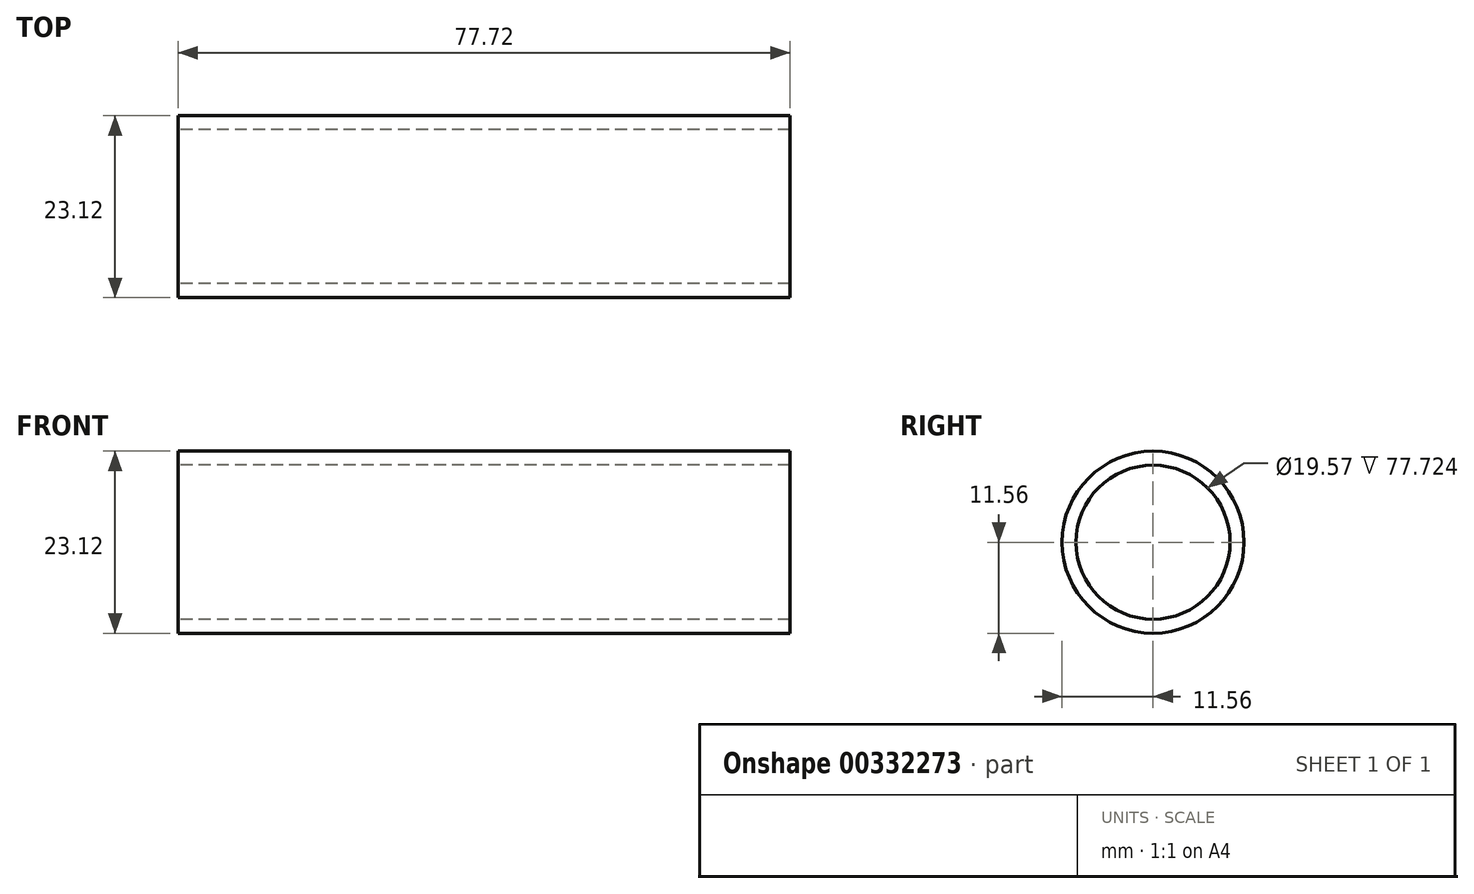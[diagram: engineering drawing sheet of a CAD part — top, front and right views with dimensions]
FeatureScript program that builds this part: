
annotation { "Feature Type Name" : "Feature", "Feature Type Description" : "" }
export const myFeature = defineFeature(function(context is Context, id is Id, definition is map)
    precondition{}
    {
        {
            var Q0;
            Q0=qCreatedBy(makeId("Right.planeOp"),FACE);
            var sketch = newSketch(context, id + "F0", { "sketchPlane" : qUnion([Q0])});
            skCircle(sketch, "E0", {"center": v(0, 0) * mm, "radius": 11.56 * mm});
            skCircle(sketch, "E1", {"center": v(0, 0) * mm, "radius": 9.78 * mm});
            skSolve(sketch);
        }
        {
            var Q0;
            Q0 = qSketchRegion(id + "F0", true);
            extrude(context, id + "F1", {"entities" : qUnion([Q0]), "depth" : 77.72 * mm});
        }
        {
            var Q0;
            Q0=qCreatedBy(makeId("Front.planeOp"),FACE);
            var sketch = newSketch(context, id + "F2", { "sketchPlane" : qUnion([Q0])});
            skFitSpline(sketch, "E2", {"points": [v(0, 0) * mm, v(-24.15, 0) * mm, v(-42.25, 0) * mm, v(-71.97, -6.86) * mm, v(-83.4, -21.81) * mm, v(-90.8, -47.03) * mm, v(-104.03, -72.85) * mm], "startDerivative": vector(-148.1, -1.36) * mm, "endDerivative": vector(-95.71, -90.34) * mm});
            skFitSpline(sketch, "E3", {"points": [v(-104.03, -72.85) * mm, v(-130.44, -80.02) * mm, v(-188.55, -80.77) * mm, v(-253.83, -80.4) * mm, v(-294.96, -72.85) * mm, v(-308.55, -49.07) * mm, v(-320.25, -18.89) * mm, v(-333.45, 0) * mm, v(-391.78, 6.19) * mm, v(-464.94, 5.77) * mm, v(-465.4, 5.77) * mm], "startDerivative": vector(-227.66, -176.53) * mm, "endDerivative": vector(-24.9, -0.34) * mm});
            skSolve(sketch);
        }
    });
